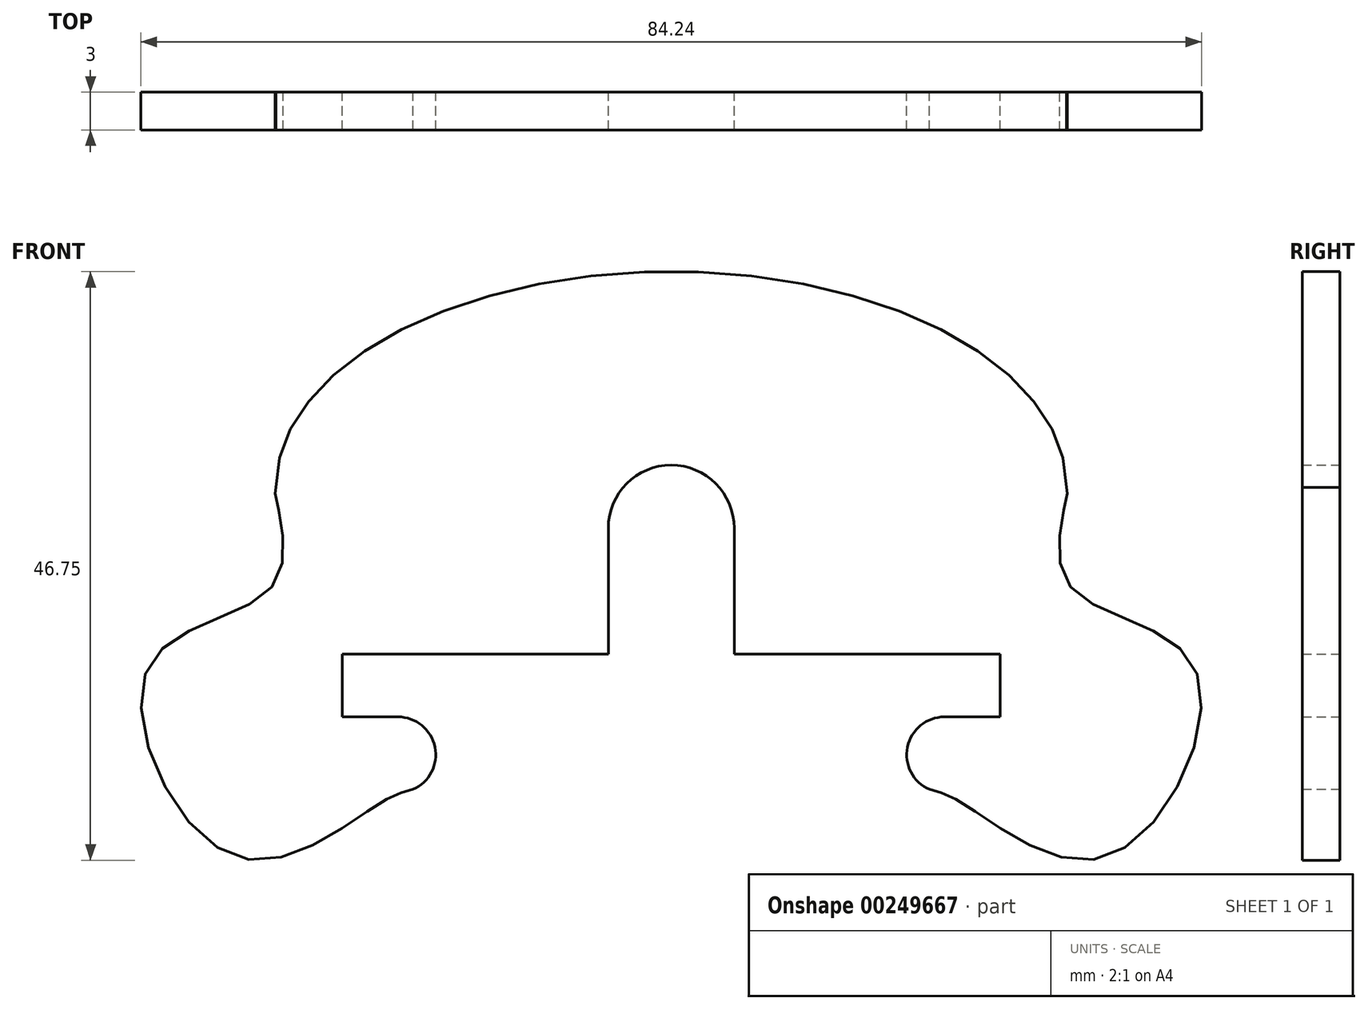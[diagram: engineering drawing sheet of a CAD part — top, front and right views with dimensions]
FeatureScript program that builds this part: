
annotation { "Feature Type Name" : "Feature", "Feature Type Description" : "" }
export const myFeature = defineFeature(function(context is Context, id is Id, definition is map)
    precondition{}
    {
        {
            var Q0;
            Q0=qCreatedBy(makeId("Front.planeOp"),FACE);
            var sketch = newSketch(context, id + "F0", { "sketchPlane" : qUnion([Q0])});
            skLineSegment(sketch, "E0", {"start": v(-26.14, -13.58) * mm, "end": v(-26.14, -8.58) * mm});
            skLineSegment(sketch, "E1", {"start": v(26.14, -13.58) * mm, "end": v(26.14, -8.58) * mm});
            skLineSegment(sketch, "E2", {"start": v(-26.14, -8.58) * mm, "end": v(-5, -8.58) * mm});
            skLineSegment(sketch, "E3", {"start": v(5, -8.58) * mm, "end": v(26.14, -8.58) * mm});
            skLineSegment(sketch, "E4", {"start": v(-26.14, -13.58) * mm, "end": v(-21.7, -13.58) * mm});
            skFitSpline(sketch, "E5", {"points": [v(-31.4, 4.66) * mm, v(-31.46, 4.18) * mm, v(-31.48, -2.92) * mm, v(-41.55, -9.6) * mm, v(-34.66, -24.65) * mm, v(-23.27, -20.52) * mm, v(-20.52, -19.33) * mm]});
            skArc(sketch, "E6", {"start": v(-20.52, -19.33) * mm, "mid": v(-18.77, -15.97) * mm, "end": v(-21.7, -13.58) * mm});
            skLineSegment(sketch, "E7", {"start": v(26.14, -13.58) * mm, "end": v(21.7, -13.58) * mm});
            skFitSpline(sketch, "E8", {"points": [v(31.4, 4.66) * mm, v(31.46, 4.18) * mm, v(31.48, -2.92) * mm, v(41.55, -9.6) * mm, v(34.66, -24.65) * mm, v(23.27, -20.52) * mm, v(20.52, -19.33) * mm]});
            skArc(sketch, "E9", {"start": v(21.7, -13.58) * mm, "mid": v(18.77, -15.97) * mm, "end": v(20.52, -19.33) * mm});
            skEllipticalArc(sketch, "E10", {});
            skLineSegment(sketch, "E11", {"start": v(5, -8.58) * mm, "end": v(5, 1.42) * mm});
            skLineSegment(sketch, "E12", {"start": v(-5, -8.58) * mm, "end": v(-5, 1.42) * mm});
            skArc(sketch, "E13", {"start": v(5, 1.42) * mm, "mid": v(0, 6.42) * mm, "end": v(-5, 1.42) * mm});
            const initialGuessF0  = {"E10": [0, 0.004662538000000041, 31.409969, 0, 0.031409969, 0.017128385000000003, 0, 3.141593]};
            skSetInitialGuess(sketch, initialGuessF0);
            skSolve(sketch);
        }
        {
            var Q0;
            Q0=makeQuery(id+"F0.imprint","IMPRINT",FACE,{"disambiguationData":[TD([[makeQuery(id+"F0.imprint","IMPRINT",EDGE,{"derivedFrom":sQuery(id+"F0.wireOp",EDGE,"E0")}),1.0]])]});
            extrude(context, id + "F1", {"entities" : qUnion([Q0]), "depth" : 3 * mm});
        }
    });
